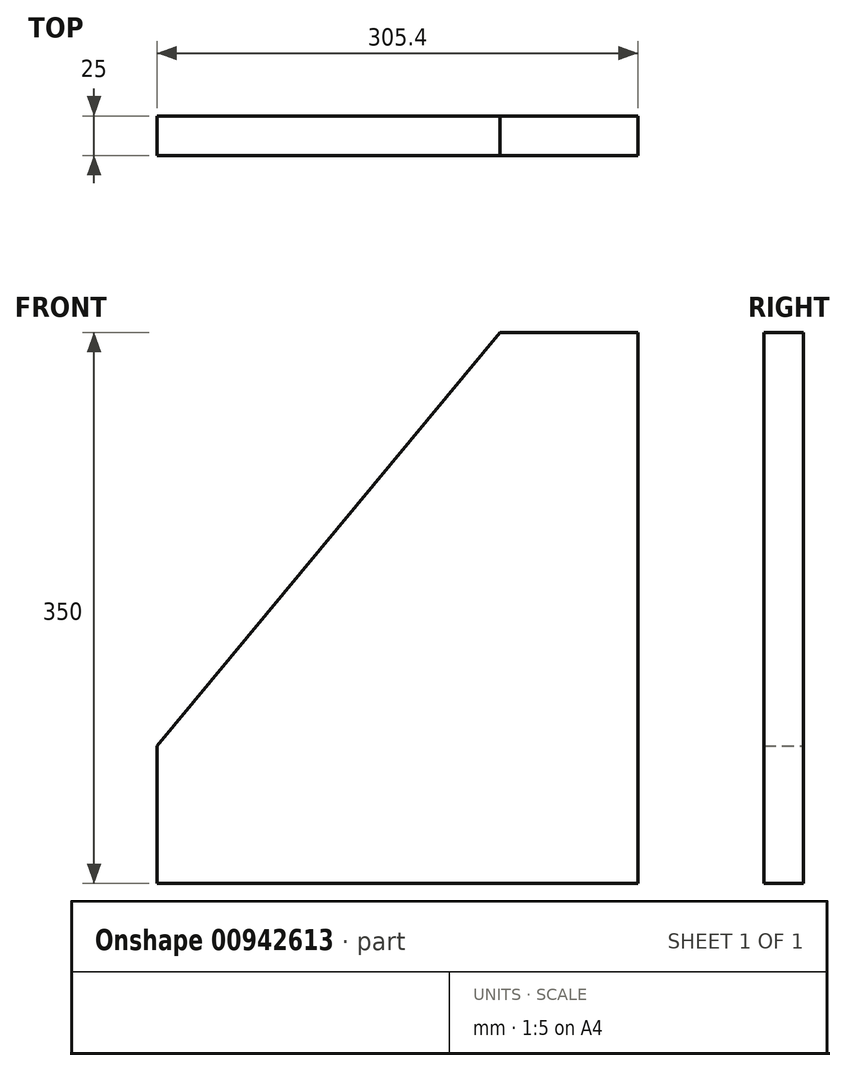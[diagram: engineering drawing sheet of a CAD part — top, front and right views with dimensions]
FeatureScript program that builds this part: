
annotation { "Feature Type Name" : "Feature", "Feature Type Description" : "" }
export const myFeature = defineFeature(function(context is Context, id is Id, definition is map)
    precondition{}
    {
        {
            var Q0;
            Q0=qCreatedBy(makeId("Front.planeOp"),FACE);
            var sketch = newSketch(context, id + "F0", { "sketchPlane" : qUnion([Q0])});
            skLineSegment(sketch, "E0.bottom", {"start": v(65.2, 175) * mm, "end": v(152.7, 175) * mm});
            skLineSegment(sketch, "E0.top", {"start": v(-152.7, -175) * mm, "end": v(152.7, -175) * mm});
            skLineSegment(sketch, "E0.left", {"start": v(-152.7, -87.5) * mm, "end": v(-152.7, -175) * mm});
            skLineSegment(sketch, "E0.right", {"start": v(152.7, 175) * mm, "end": v(152.7, -175) * mm});
            skLineSegment(sketch, "E1", {"start": v(-152.7, -87.5) * mm, "end": v(65.2, 175) * mm});
            skSolve(sketch);
        }
        {
            var Q0;
            Q0 = qSketchRegion(id + "F0", true);
            extrude(context, id + "F1", {"entities" : qUnion([Q0]), "depth" : 25 * mm, "offsetDistance" : 25 * mm});
        }
    });
